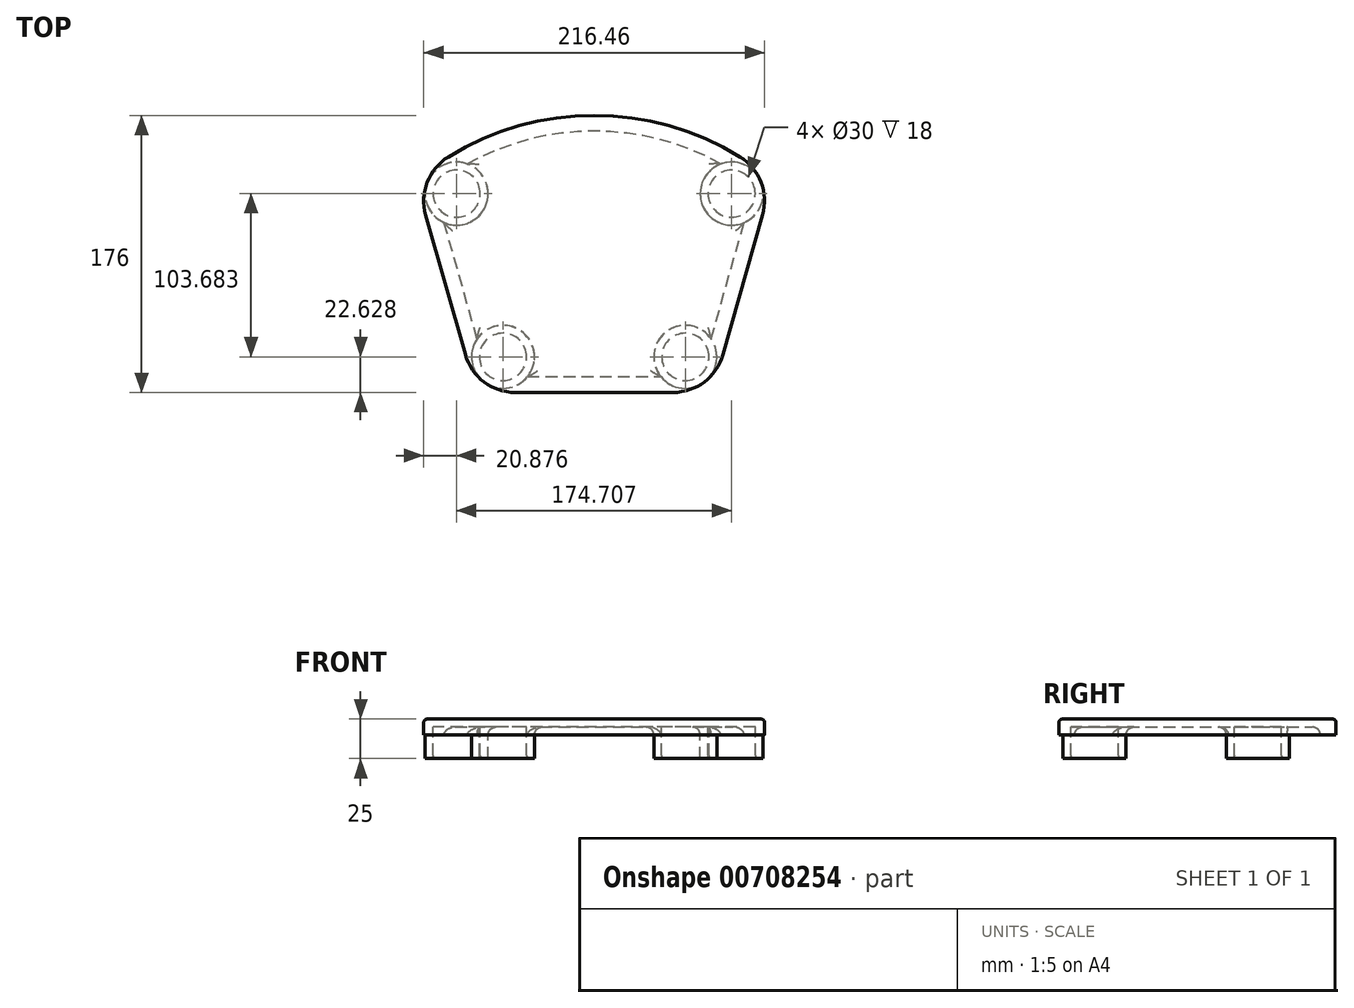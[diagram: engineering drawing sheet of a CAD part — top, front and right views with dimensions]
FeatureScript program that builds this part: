
annotation { "Feature Type Name" : "Feature", "Feature Type Description" : "" }
export const myFeature = defineFeature(function(context is Context, id is Id, definition is map)
    precondition{}
    {
        {
            var Q0;
            Q0=qCreatedBy(makeId("Top.planeOp"),FACE);
            var sketch = newSketch(context, id + "F0", { "sketchPlane" : qUnion([Q0])});
            skLineSegment(sketch, "E0", {"start": v(-50.07, 0) * mm, "end": v(0, 0) * mm});
            skLineSegment(sketch, "E1", {"start": v(81.81, 23.98) * mm, "end": v(106.98, 112.6) * mm});
            skLineSegment(sketch, "E2", {"start": v(0, 0) * mm, "end": v(50.07, 0) * mm});
            skLineSegment(sketch, "E3", {"start": v(-81.81, 23.98) * mm, "end": v(-106.98, 112.6) * mm});
            skArc(sketch, "E4", {"start": v(92.6, 149.67) * mm, "mid": v(0, 176) * mm, "end": v(-92.6, 149.67) * mm});
            skLineSegment(sketch, "E5", {"start": v(0, 0) * mm, "end": v(0, 176) * mm, "construction": true});
            skLineSegment(sketch, "E6", {"start": v(-113.26, 134.71) * mm, "end": v(0, 0) * mm, "construction": true});
            skLineSegment(sketch, "E7", {"start": v(113.26, 134.71) * mm, "end": v(0, 0) * mm, "construction": true});
            skPoint(sketch, "E8.visualSharp", {"position": v(-75, 0) * mm});
            skArc(sketch, "E8.filletArc", {"start": v(-81.81, 23.98) * mm, "mid": v(-69.96, 6.67) * mm, "end": v(-50.07, 0) * mm});
            skPoint(sketch, "E9.visualSharp", {"position": v(75, 0) * mm});
            skArc(sketch, "E9.filletArc", {"start": v(50.07, 0) * mm, "mid": v(69.96, 6.67) * mm, "end": v(81.81, 23.98) * mm});
            skPoint(sketch, "E10.visualSharp", {"position": v(113.26, 134.71) * mm});
            skArc(sketch, "E10.filletArc", {"start": v(106.98, 112.6) * mm, "mid": v(106, 133.54) * mm, "end": v(92.6, 149.67) * mm});
            skPoint(sketch, "E11.visualSharp", {"position": v(-113.26, 134.71) * mm});
            skArc(sketch, "E11.filletArc", {"start": v(-92.6, 149.67) * mm, "mid": v(-106, 133.54) * mm, "end": v(-106.98, 112.6) * mm});
            skLineSegment(sketch, "E12.1", {"start": v(72.2, 26.72) * mm, "end": v(95.26, 107.94) * mm});
            skArc(sketch, "E12.2", {"start": v(80.58, 145.13) * mm, "mid": v(0, 166) * mm, "end": v(-80.58, 145.13) * mm});
            skArc(sketch, "E12.3", {"start": v(50.07, 10) * mm, "mid": v(63.93, 14.65) * mm, "end": v(72.2, 26.72) * mm});
            skLineSegment(sketch, "E12.4", {"start": v(0, 10) * mm, "end": v(50.07, 10) * mm});
            skLineSegment(sketch, "E12.6", {"start": v(-72.2, 26.72) * mm, "end": v(-95.26, 107.94) * mm});
            skArc(sketch, "E12.7", {"start": v(-72.2, 26.72) * mm, "mid": v(-63.93, 14.65) * mm, "end": v(-50.07, 10) * mm});
            skLineSegment(sketch, "E12.8", {"start": v(-50.07, 10) * mm, "end": v(0, 10) * mm});
            skCircle(sketch, "E13", {"center": v(-87.35, 126.31) * mm, "radius": 15 * mm});
            skLineSegment(sketch, "E14", {"start": v(-75.23, 121.6) * mm, "end": v(-106, 133.54) * mm, "construction": true});
            skLineSegment(sketch, "E15", {"start": v(-106, 133.54) * mm, "end": v(-92.6, 149.67) * mm, "construction": true});
            skLineSegment(sketch, "E16", {"start": v(-106, 133.54) * mm, "end": v(-106.98, 112.6) * mm, "construction": true});
            skCircle(sketch, "E17", {"center": v(-87.35, 126.31) * mm, "radius": 20 * mm});
            skLineSegment(sketch, "E18", {"start": v(75.23, 121.6) * mm, "end": v(106, 133.54) * mm, "construction": true});
            skCircle(sketch, "E19", {"center": v(87.35, 126.31) * mm, "radius": 15 * mm});
            skCircle(sketch, "E20", {"center": v(87.35, 126.31) * mm, "radius": 20 * mm});
            skLineSegment(sketch, "E21", {"start": v(-81.81, 23.98) * mm, "end": v(-50.07, 33) * mm, "construction": true});
            skLineSegment(sketch, "E22", {"start": v(-50.07, 33) * mm, "end": v(-50.07, 0) * mm, "construction": true});
            skLineSegment(sketch, "E23", {"start": v(-50.07, 33) * mm, "end": v(-69.96, 6.67) * mm, "construction": true});
            skCircle(sketch, "E24", {"center": v(-57.9, 22.63) * mm, "radius": 15 * mm});
            skCircle(sketch, "E25", {"center": v(-57.9, 22.63) * mm, "radius": 20 * mm});
            skLineSegment(sketch, "E26", {"start": v(50.07, 0) * mm, "end": v(50.07, 33) * mm, "construction": true});
            skLineSegment(sketch, "E27", {"start": v(50.07, 33) * mm, "end": v(81.81, 23.98) * mm, "construction": true});
            skLineSegment(sketch, "E28", {"start": v(50.07, 33) * mm, "end": v(69.96, 6.67) * mm, "construction": true});
            skCircle(sketch, "E29", {"center": v(57.9, 22.63) * mm, "radius": 15 * mm});
            skCircle(sketch, "E30", {"center": v(57.9, 22.63) * mm, "radius": 20 * mm});
            skSolve(sketch);
        }
        {
            var Q0;
            {var subQ4=sQuery(id+"F0.wireOp",EDGE,"E19");var subQ5=makeQuery(id+"F0.imprint","IMPRINT",VERTEX,{"disambiguationData":[OD(0.0)],"derivedFrom":subQ4});Q0=makeQuery(id+"F0.imprint","IMPRINT",FACE,{"disambiguationData":[TD([[makeQuery(id+"F0.imprint","IMPRINT",EDGE,{"disambiguationData":[TD([[subQ5,1.0]])],"derivedFrom":subQ4}),-1.0]])]});}
            var Q1;
            {var subQ0=sQuery(id+"F0.wireOp",EDGE,"E24");var subQ1=sQuery(id+"F0.wireOp",EDGE,"E12.6");var subQ2=makeQuery(id+"F0.imprint","INTERSECT",VERTEX,{"derivedFrom":[subQ1,subQ0]});Q1=makeQuery(id+"F0.imprint","IMPRINT",FACE,{"disambiguationData":[TD([[makeQuery(id+"F0.imprint","IMPRINT",EDGE,{"disambiguationData":[TD([[subQ2,-1.0]])],"derivedFrom":subQ1}),-1.0]])]});}
            var Q2;
            {var subQ4=sQuery(id+"F0.wireOp",EDGE,"E29");var subQ5=sQuery(id+"F0.wireOp",EDGE,"E12.1");var subQ6=makeQuery(id+"F0.imprint","INTERSECT",VERTEX,{"derivedFrom":[subQ5,subQ4]});Q2=makeQuery(id+"F0.imprint","IMPRINT",FACE,{"disambiguationData":[TD([[makeQuery(id+"F0.imprint","IMPRINT",EDGE,{"disambiguationData":[TD([[subQ6,-1.0]])],"derivedFrom":subQ5}),-1.0]])]});}
            var Q3;
            {var subQ0=sQuery(id+"F0.wireOp",EDGE,"E12.3");Q3=makeQuery(id+"F0.imprint","IMPRINT",FACE,{"disambiguationData":[TD([[makeQuery(id+"F0.imprint","IMPRINT",EDGE,{"derivedFrom":subQ0}),1.0]])]});}
            var Q4;
            {var subQ0=sQuery(id+"F0.wireOp",EDGE,"E12.3");Q4=makeQuery(id+"F0.imprint","IMPRINT",FACE,{"disambiguationData":[TD([[makeQuery(id+"F0.imprint","IMPRINT",EDGE,{"derivedFrom":subQ0}),-1.0]])]});}
            var Q5;
            {var subQ1=sQuery(id+"F0.wireOp",EDGE,"E3");Q5=makeQuery(id+"F0.imprint","IMPRINT",FACE,{"disambiguationData":[TD([[makeQuery(id+"F0.imprint","IMPRINT",EDGE,{"derivedFrom":subQ1}),-1.0]])]});}
            var Q6;
            {var subQ0=sQuery(id+"F0.wireOp",EDGE,"E12.7");Q6=makeQuery(id+"F0.imprint","IMPRINT",FACE,{"disambiguationData":[TD([[makeQuery(id+"F0.imprint","IMPRINT",EDGE,{"derivedFrom":subQ0}),-1.0]])]});}
            var Q7;
            {var subQ0=sQuery(id+"F0.wireOp",EDGE,"E12.7");Q7=makeQuery(id+"F0.imprint","IMPRINT",FACE,{"disambiguationData":[TD([[makeQuery(id+"F0.imprint","IMPRINT",EDGE,{"derivedFrom":subQ0}),1.0]])]});}
            var Q8;
            {var subQ1=sQuery(id+"F0.wireOp",EDGE,"E0");Q8=makeQuery(id+"F0.imprint","IMPRINT",FACE,{"disambiguationData":[TD([[makeQuery(id+"F0.imprint","IMPRINT",EDGE,{"derivedFrom":subQ1}),1.0]])]});}
            var Q9;
            {var subQ7=sQuery(id+"F0.wireOp",EDGE,"E1");Q9=makeQuery(id+"F0.imprint","IMPRINT",FACE,{"disambiguationData":[TD([[makeQuery(id+"F0.imprint","IMPRINT",EDGE,{"derivedFrom":subQ7}),1.0]])]});}
            var Q10;
            {var subQ0=sQuery(id+"F0.wireOp",EDGE,"E29");var subQ1=sQuery(id+"F0.wireOp",EDGE,"E12.1");var subQ2=makeQuery(id+"F0.imprint","INTERSECT",VERTEX,{"derivedFrom":[subQ1,subQ0]});Q10=makeQuery(id+"F0.imprint","IMPRINT",FACE,{"disambiguationData":[TD([[makeQuery(id+"F0.imprint","IMPRINT",EDGE,{"disambiguationData":[TD([[subQ2,-1.0]])],"derivedFrom":subQ1}),1.0]])]});}
            var Q11;
            {var subQ2=sQuery(id+"F0.wireOp",EDGE,"E12.6");var subQ4=sQuery(id+"F0.wireOp",EDGE,"E24");var subQ5=makeQuery(id+"F0.imprint","INTERSECT",VERTEX,{"derivedFrom":[subQ2,subQ4]});Q11=makeQuery(id+"F0.imprint","IMPRINT",FACE,{"disambiguationData":[TD([[makeQuery(id+"F0.imprint","IMPRINT",EDGE,{"disambiguationData":[TD([[subQ5,-1.0]])],"derivedFrom":subQ2}),1.0]])]});}
            var Q12;
            {var subQ2=sQuery(id+"F0.wireOp",EDGE,"E4");Q12=makeQuery(id+"F0.imprint","IMPRINT",FACE,{"disambiguationData":[TD([[makeQuery(id+"F0.imprint","IMPRINT",EDGE,{"derivedFrom":subQ2}),1.0]])]});}
            var Q13;
            {var subQ0=sQuery(id+"F0.wireOp",EDGE,"E19");var subQ1=makeQuery(id+"F0.imprint","IMPRINT",VERTEX,{"disambiguationData":[OD(0.0)],"derivedFrom":subQ0});Q13=makeQuery(id+"F0.imprint","IMPRINT",FACE,{"disambiguationData":[TD([[makeQuery(id+"F0.imprint","IMPRINT",EDGE,{"disambiguationData":[TD([[subQ1,1.0]])],"derivedFrom":subQ0}),1.0]])]});}
            var Q14;
            {var subQ0=sQuery(id+"F0.wireOp",EDGE,"E13");var subQ1=makeQuery(id+"F0.imprint","IMPRINT",VERTEX,{"disambiguationData":[OD(0.0)],"derivedFrom":subQ0});Q14=makeQuery(id+"F0.imprint","IMPRINT",FACE,{"disambiguationData":[TD([[makeQuery(id+"F0.imprint","IMPRINT",EDGE,{"disambiguationData":[TD([[subQ1,-1.0]])],"derivedFrom":subQ0}),1.0]])]});}
            var Q15;
            {var subQ4=sQuery(id+"F0.wireOp",EDGE,"E13");var subQ5=makeQuery(id+"F0.imprint","IMPRINT",VERTEX,{"disambiguationData":[OD(0.0)],"derivedFrom":subQ4});Q15=makeQuery(id+"F0.imprint","IMPRINT",FACE,{"disambiguationData":[TD([[makeQuery(id+"F0.imprint","IMPRINT",EDGE,{"disambiguationData":[TD([[subQ5,-1.0]])],"derivedFrom":subQ4}),-1.0]])]});}
            var Q16;
            {var subQ12=sQuery(id+"F0.wireOp",EDGE,"E12.2");Q16=makeQuery(id+"F0.imprint","IMPRINT",FACE,{"disambiguationData":[TD([[makeQuery(id+"F0.imprint","IMPRINT",EDGE,{"derivedFrom":subQ12}),1.0]])]});}
            extrude(context, id + "F1", {"entities" : qUnion([Q0, Q1, Q2, Q3, Q4, Q5, Q6, Q7, Q8, Q9, Q10, Q11, Q12, Q13, Q14, Q15, Q16]), "oppositeDirection" : true, "depth" : 5 * mm, "offsetDistance" : 25 * mm});
        }
        {
            var Q0;
            {var subQ4=sQuery(id+"F0.wireOp",EDGE,"E13");var subQ5=makeQuery(id+"F0.imprint","IMPRINT",VERTEX,{"disambiguationData":[OD(0.0)],"derivedFrom":subQ4});Q0=makeQuery(id+"F0.imprint","IMPRINT",FACE,{"disambiguationData":[TD([[makeQuery(id+"F0.imprint","IMPRINT",EDGE,{"disambiguationData":[TD([[subQ5,-1.0]])],"derivedFrom":subQ4}),-1.0]])]});}
            var Q1;
            {var subQ0=sQuery(id+"F0.wireOp",EDGE,"E24");var subQ1=sQuery(id+"F0.wireOp",EDGE,"E12.6");var subQ2=makeQuery(id+"F0.imprint","INTERSECT",VERTEX,{"derivedFrom":[subQ1,subQ0]});Q1=makeQuery(id+"F0.imprint","IMPRINT",FACE,{"disambiguationData":[TD([[makeQuery(id+"F0.imprint","IMPRINT",EDGE,{"disambiguationData":[TD([[subQ2,-1.0]])],"derivedFrom":subQ1}),-1.0]])]});}
            var Q2;
            {var subQ2=sQuery(id+"F0.wireOp",EDGE,"E12.6");var subQ4=sQuery(id+"F0.wireOp",EDGE,"E24");var subQ5=makeQuery(id+"F0.imprint","INTERSECT",VERTEX,{"derivedFrom":[subQ2,subQ4]});Q2=makeQuery(id+"F0.imprint","IMPRINT",FACE,{"disambiguationData":[TD([[makeQuery(id+"F0.imprint","IMPRINT",EDGE,{"disambiguationData":[TD([[subQ5,-1.0]])],"derivedFrom":subQ2}),1.0]])]});}
            var Q3;
            {var subQ4=sQuery(id+"F0.wireOp",EDGE,"E29");var subQ5=sQuery(id+"F0.wireOp",EDGE,"E12.1");var subQ6=makeQuery(id+"F0.imprint","INTERSECT",VERTEX,{"derivedFrom":[subQ5,subQ4]});Q3=makeQuery(id+"F0.imprint","IMPRINT",FACE,{"disambiguationData":[TD([[makeQuery(id+"F0.imprint","IMPRINT",EDGE,{"disambiguationData":[TD([[subQ6,-1.0]])],"derivedFrom":subQ5}),-1.0]])]});}
            var Q4;
            {var subQ0=sQuery(id+"F0.wireOp",EDGE,"E29");var subQ1=sQuery(id+"F0.wireOp",EDGE,"E12.1");var subQ2=makeQuery(id+"F0.imprint","INTERSECT",VERTEX,{"derivedFrom":[subQ1,subQ0]});Q4=makeQuery(id+"F0.imprint","IMPRINT",FACE,{"disambiguationData":[TD([[makeQuery(id+"F0.imprint","IMPRINT",EDGE,{"disambiguationData":[TD([[subQ2,-1.0]])],"derivedFrom":subQ1}),1.0]])]});}
            var Q5;
            {var subQ4=sQuery(id+"F0.wireOp",EDGE,"E19");var subQ5=makeQuery(id+"F0.imprint","IMPRINT",VERTEX,{"disambiguationData":[OD(0.0)],"derivedFrom":subQ4});Q5=makeQuery(id+"F0.imprint","IMPRINT",FACE,{"disambiguationData":[TD([[makeQuery(id+"F0.imprint","IMPRINT",EDGE,{"disambiguationData":[TD([[subQ5,1.0]])],"derivedFrom":subQ4}),-1.0]])]});}
            extrude(context, id + "F2", {"entities" : qUnion([Q0, Q1, Q2, Q3, Q4, Q5]), "operationType" : NewBodyOperationType.ADD, "oppositeDirection" : true, "depth" : 25 * mm, "offsetDistance" : 25 * mm});
        }
        {
            var Q0;
            {var subQ1=sQuery(id+"F0.wireOp",EDGE,"E0");Q0=makeQuery(id+"F0.imprint","IMPRINT",FACE,{"disambiguationData":[TD([[makeQuery(id+"F0.imprint","IMPRINT",EDGE,{"derivedFrom":subQ1}),1.0]])]});}
            var Q1;
            {var subQ1=sQuery(id+"F0.wireOp",EDGE,"E3");Q1=makeQuery(id+"F0.imprint","IMPRINT",FACE,{"disambiguationData":[TD([[makeQuery(id+"F0.imprint","IMPRINT",EDGE,{"derivedFrom":subQ1}),-1.0]])]});}
            var Q2;
            {var subQ2=sQuery(id+"F0.wireOp",EDGE,"E4");Q2=makeQuery(id+"F0.imprint","IMPRINT",FACE,{"disambiguationData":[TD([[makeQuery(id+"F0.imprint","IMPRINT",EDGE,{"derivedFrom":subQ2}),1.0]])]});}
            var Q3;
            {var subQ7=sQuery(id+"F0.wireOp",EDGE,"E1");Q3=makeQuery(id+"F0.imprint","IMPRINT",FACE,{"disambiguationData":[TD([[makeQuery(id+"F0.imprint","IMPRINT",EDGE,{"derivedFrom":subQ7}),1.0]])]});}
            extrude(context, id + "F3", {"entities" : qUnion([Q0, Q1, Q2, Q3]), "operationType" : NewBodyOperationType.ADD, "oppositeDirection" : true, "depth" : 10 * mm, "offsetDistance" : 25 * mm});
        }
        {
            var Q0;
            Q0=makeQuery(id+"F1.opExtrude","CAP_FACE",FACE,{"disambiguationData":[OSD([sQuery(id+"F0.wireOp",EDGE,"E0"),sQuery(id+"F0.wireOp",EDGE,"E1"),sQuery(id+"F0.wireOp",EDGE,"E2"),sQuery(id+"F0.wireOp",EDGE,"E3"),sQuery(id+"F0.wireOp",EDGE,"E4"),sQuery(id+"F0.wireOp",EDGE,"E8.filletArc"),sQuery(id+"F0.wireOp",EDGE,"E9.filletArc"),sQuery(id+"F0.wireOp",EDGE,"E10.filletArc"),sQuery(id+"F0.wireOp",EDGE,"E11.filletArc")])],"isStart":true});
            var Q1;
            Q1=makeQuery(id+"F2.opExtrude","CAP_EDGE",EDGE,{"disambiguationData":[OSD([sQuery(id+"F0.wireOp",EDGE,"E24")])],"isStart":false});
            var Q2;
            Q2=makeQuery(id+"F2.opExtrude","CAP_EDGE",EDGE,{"disambiguationData":[OSD([sQuery(id+"F0.wireOp",EDGE,"E29")])],"isStart":false});
            var Q3;
            Q3=makeQuery(id+"F2.opExtrude","CAP_EDGE",EDGE,{"disambiguationData":[OSD([sQuery(id+"F0.wireOp",EDGE,"E19")])],"isStart":false});
            var Q4;
            Q4=makeQuery(id+"F2.opExtrude","CAP_EDGE",EDGE,{"disambiguationData":[OSD([sQuery(id+"F0.wireOp",EDGE,"E13")])],"isStart":false});
            fillet(context, id + "F4", {"entities" : qUnion([Q0, Q1, Q2, Q3, Q4]), "radius" : 2 * mm, "tangentPropagation" : true, "allowEdgeOverflow" : false});
        }
        {
            var Q0;
            {var subQ0=sQuery(id+"F0.wireOp",EDGE,"E11.filletArc");var subQ1=sQuery(id+"F0.wireOp",EDGE,"E10.filletArc");var subQ2=sQuery(id+"F0.wireOp",EDGE,"E9.filletArc");var subQ3=sQuery(id+"F0.wireOp",EDGE,"E8.filletArc");var subQ4=sQuery(id+"F0.wireOp",EDGE,"E2");var subQ5=sQuery(id+"F0.wireOp",EDGE,"E0");var subQ6=sQuery(id+"F0.wireOp",EDGE,"E1");var subQ7=sQuery(id+"F0.wireOp",EDGE,"E3");var subQ8=sQuery(id+"F0.wireOp",EDGE,"E4");Q0=makeQuery(id+"F2.boolean.opBoolean","SPLIT",FACE,{"disambiguationData":[TD([makeQuery(id+"F1.opExtrude","SWEPT_FACE",FACE,{"disambiguationData":[OSD([subQ6])]})])],"derivedFrom":makeQuery(id+"F1.opExtrude","CAP_FACE",FACE,{"disambiguationData":[OSD([subQ5,subQ6,subQ4,subQ7,subQ8,subQ3,subQ2,subQ1,subQ0])],"isStart":false})});}
            fillet(context, id + "F5", {"entities" : qUnion([Q0]), "radius" : 5 * mm, "tangentPropagation" : true, "allowEdgeOverflow" : false});
        }
    });
